# Revit family: QF_GIORIK_PGI910
name_source: partatom
category: Specialty Equipment
revit_build: Autodesk Revit 2014 (Build: 20140709_2115(x64)
units: mm (PartAtom-declared; Revit-internal decimal feet)

## types (1)
- PGI910
    Assembly Code = E1090320
    Cold Water Maximum Pressure = 50000.0 Pa
    Cold Water Minimum Pressure = 20000.0 Pa
    Cold Water Size = 1/2"
    Cold Water Temperature Recommended = 0 °C
    Description = 100 LITRE GAS BOILING PAN - INDIRECT HEATING VERSION.
    Gas Input = 21000 W
    Gas KW = 21
    Gas Size = 1"
    Hot Water Connection Height = 150 mm
    Hot Water Consumption = 0.0 L/s
    Hot Water Flow = 0.0 L/s
    Hot Water Maximum Pressure = 50000.0 Pa
    Hot Water Minimum Pressure = 20000.0 Pa
    Hot Water Size = 1/2"
    Hot Water Temperature = 0 °C
    Indirect Waste Flow = 0.0 L/s
    Indirect Waste Size = 1"
    Manufacturer = GIORIK
    Model = PGI910
    URL = www.giorik.com
    URL Cutsheet = www.giorik.com
    Weight in Pounds = 396.8316

## geometry (parser evidence)
native form markers: Blend x14, Sweep x2
no freeform markers — native parametric forms only
